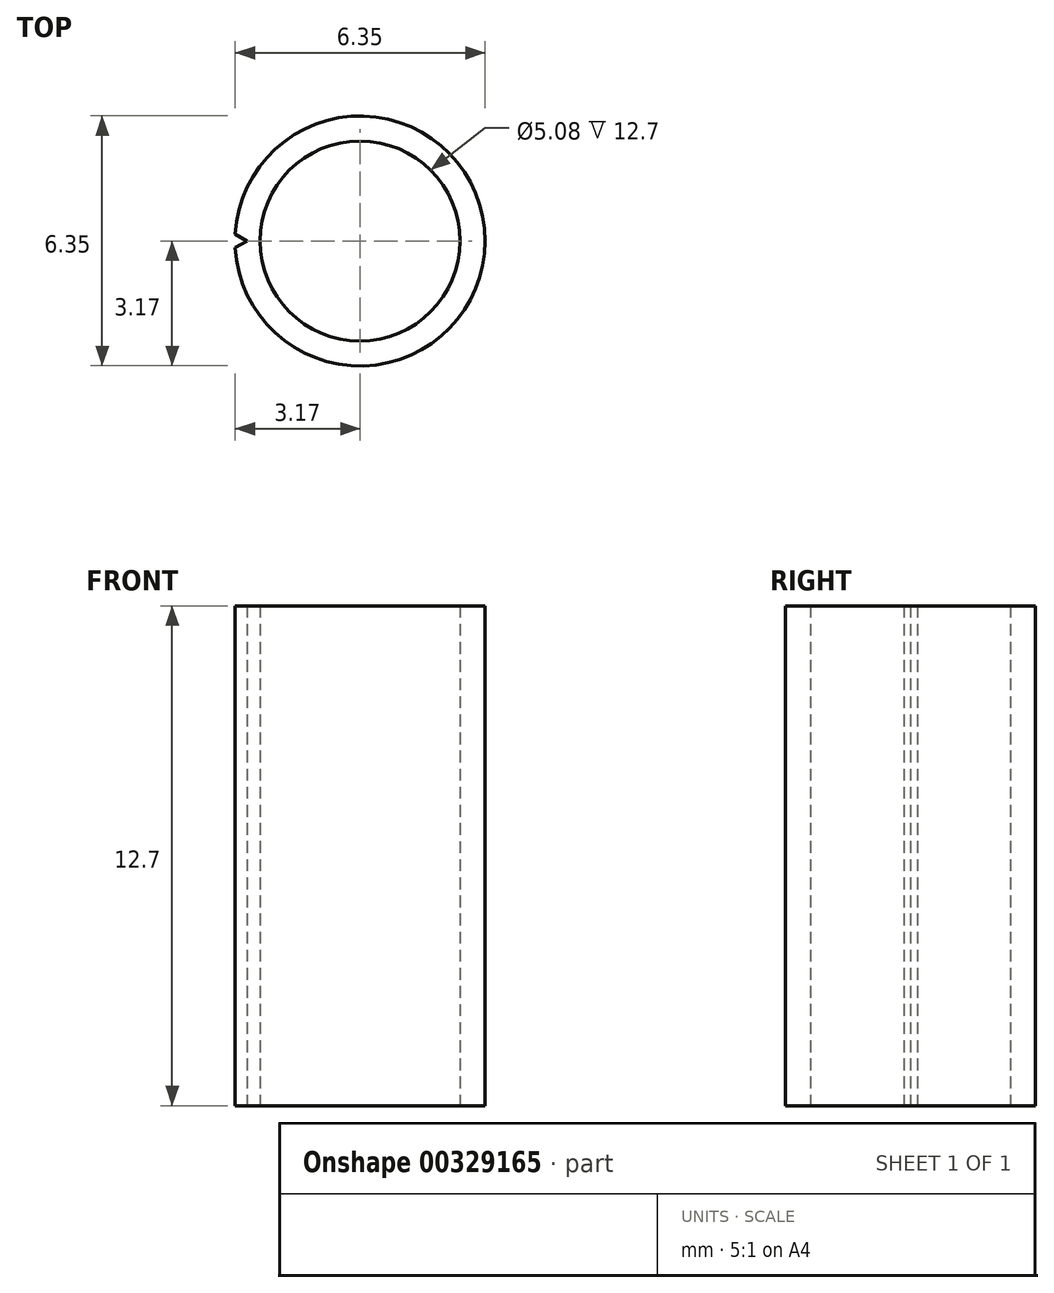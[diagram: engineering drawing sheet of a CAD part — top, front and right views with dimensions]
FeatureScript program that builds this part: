
annotation { "Feature Type Name" : "Feature", "Feature Type Description" : "" }
export const myFeature = defineFeature(function(context is Context, id is Id, definition is map)
    precondition{}
    {
        {
            var Q0;
            Q0=qCreatedBy(makeId("Top.planeOp"),FACE);
            var sketch = newSketch(context, id + "F0", { "sketchPlane" : qUnion([Q0])});
            skArc(sketch, "E0", {"start": v(-3.17, -0.17) * mm, "mid": v(3.18, 0) * mm, "end": v(-3.17, 0.17) * mm});
            skCircle(sketch, "E1", {"center": v(0, 0) * mm, "radius": 2.54 * mm});
            skLineSegment(sketch, "E2", {"start": v(-2.54, 0) * mm, "end": v(-3.18, 0) * mm, "construction": true});
            skLineSegment(sketch, "E3", {"start": v(-2.87, 0) * mm, "end": v(-3.17, 0.17) * mm});
            skPoint(sketch, "E4.orphan", {"position": v(-4.16, 0) * mm});
            skPoint(sketch, "E5.orphan", {"position": v(-1.59, 0) * mm});
            skLineSegment(sketch, "E6.MirrorCS", {"start": v(-2.87, 0) * mm, "end": v(-3.17, -0.17) * mm});
            skSolve(sketch);
        }
        {
            var Q0;
            Q0=makeQuery(id+"F0.imprint","IMPRINT",FACE,{"disambiguationData":[TD([[makeQuery(id+"F0.imprint","IMPRINT",EDGE,{"derivedFrom":sQuery(id+"F0.wireOp",EDGE,"E0")}),1.0]])]});
            extrude(context, id + "F1", {"entities" : qUnion([Q0]), "depth" : 12.7 * mm});
        }
    });
